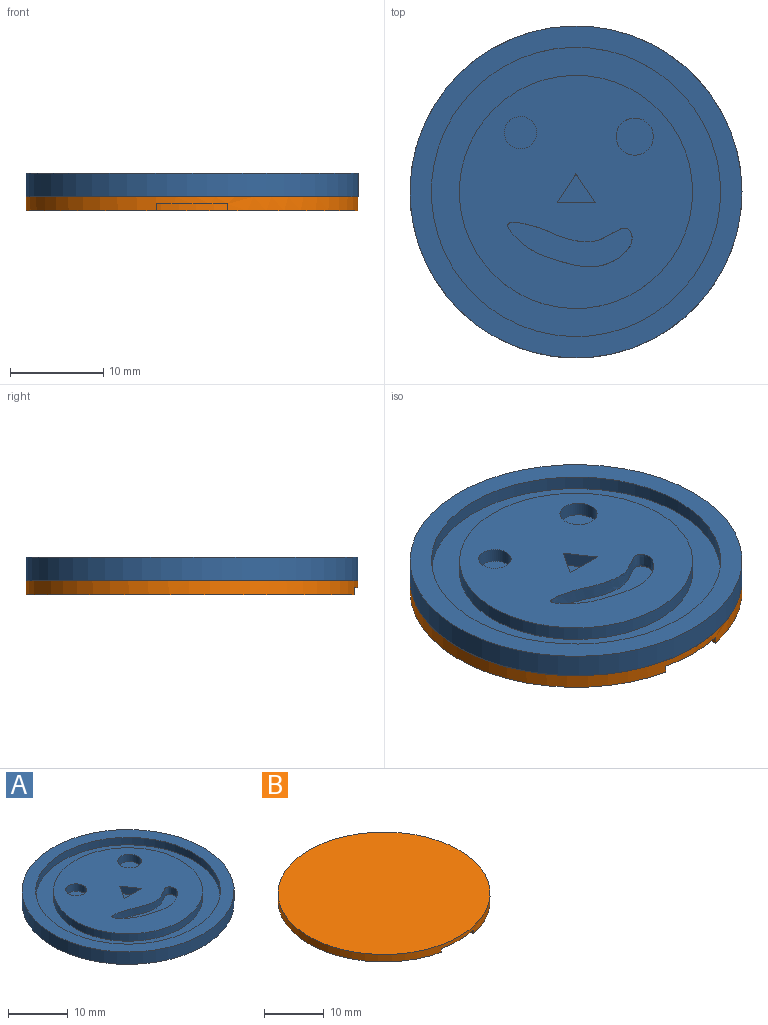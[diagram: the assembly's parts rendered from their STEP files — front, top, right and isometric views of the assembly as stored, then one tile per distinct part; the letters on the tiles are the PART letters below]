
ASSEMBLY  parts=2 mates=1
PART A: 17 faces, bbox 35.6x35.6x2.5 mm
  f0: cylinder r=17.78mm len=35.56mm, axis (0,0,-1), area 283.8mm2, adj f1,f2
  f1: plane 35.56x35.56mm, normal (0,0,1), area 239mm2, adj f0,f3
  f2: plane 35.56x35.56mm, normal (0,0,-1), area 993.1mm2, adj f0
  f3: cylinder r=15.49mm len=30.99mm, axis (0,0,1), area 148.4mm2, adj f1,f4
  f4: plane 30.99x30.99mm, normal (0,0,1), area 264.3mm2, adj f3,f6
  f5: plane 24.98x24.98mm, normal (0,0,1), area 427.8mm2, adj f6,f7,f8,f9,f10,f11,f12
  f6: cylinder r=12.49mm len=24.98mm, axis (0,0,1), area 119.6mm2, adj f4,f5
  f7: plane 3.05x2.03mm, normal (0.83,-0.55,0), area 5.6mm2, adj f5,f8,f9,f14
  f8: plane 3.05x2.07mm, normal (-0.83,-0.56,0), area 5.6mm2, adj f5,f7,f9,f14
  f9: plane 4.1x1.52mm, normal (0,1,0), area 6.2mm2, adj f5,f7,f8,f14
  f10: extruded ~13.3x4.76mm, area 47.1mm2, adj f5,f15
  f11: cylinder r=1.99mm len=3.98mm, axis (0,0,1), area 19mm2, adj f5,f13
  f12: cylinder r=1.74mm len=3.48mm, axis (0,0,1), area 16.6mm2, adj f5,f16
  f13: plane 3.98x3.98mm, normal (0,0,1), area 12.4mm2, adj f11
  f14: plane 4.1x3.05mm, normal (0,0,1), area 6.3mm2, adj f7,f8,f9
  f15: plane 13.65x5.11mm, normal (0,0,1), area 33.9mm2, adj f10
  f16: plane 3.48x3.48mm, normal (0,0,1), area 9.5mm2, adj f12
PART B: 170 faces, bbox 35.6x35.6x1.5 mm
  f0: plane 30.99x30.99mm, normal (0,0,-1), area 549.6mm2, adj f4,f5,f6,f7,f8,f9,f10,f11
  f1: plane 35.56x35.15mm, normal (0,0,-1), area 175mm2, adj f2,f165,f167,f169
  f2: cylinder r=17.78mm len=35.56mm, axis (0,0,-1), area 164.4mm2, adj f1,f3,f165,f167,f168
  f3: plane 35.56x35.56mm, normal (0,0,1), area 993.1mm2, adj f2
  f4: plane 1.49x0.76mm, normal (0,-1,0), area 1.1mm2, adj f0,f5,f15,f16
  f5: plane 7.05x0.76mm, normal (-1,0,0), area 5.4mm2, adj f0,f4,f6,f16
  f6: plane 1.49x0.76mm, normal (0,1,0), area 1.1mm2, adj f0,f5,f7,f16
  f7: plane 2.76x0.76mm, normal (1,0,0), area 2.1mm2, adj f0,f6,f8,f16
  f8: plane 2.79x0.76mm, normal (0,1,0), area 2.1mm2, adj f0,f7,f9,f16
  f9: plane 2.76x0.76mm, normal (-1,0,0), area 2.1mm2, adj f0,f8,f10,f16
  f10: plane 1.5x0.76mm, normal (0,1,0), area 1.1mm2, adj f0,f9,f11,f16
  f11: plane 7.05x0.76mm, normal (1,0,0), area 5.4mm2, adj f0,f10,f12,f16
  f12: plane 1.5x0.76mm, normal (0,-1,0), area 1.1mm2, adj f0,f11,f13,f16
  f13: plane 3.04x0.76mm, normal (-1,0,0), area 2.3mm2, adj f0,f12,f14,f16
  f14: plane 2.79x0.76mm, normal (0,-1,0), area 2.1mm2, adj f0,f13,f15,f16
  f15: plane 3.04x0.76mm, normal (1,0,0), area 2.3mm2, adj f0,f4,f14,f16
  f16: plane 7.05x5.78mm, normal (0,0,-1), area 24.5mm2, adj f4,f5,f6,f7,f8,f9,f10,f11
  f17: plane 7.05x0.76mm, normal (-1,0,0), area 5.4mm2, adj f0,f18,f41,f42
  f18: plane 2.19x0.76mm, normal (0,1,0), area 1.7mm2, adj f0,f17,f19,f42
  f19: extruded ~2.18x0.76mm, area 1.7mm2, adj f0,f18,f20,f42
  f20: extruded ~1.36x0.76mm, area 1.2mm2, adj f0,f19,f21,f42
  f21: extruded ~1.04x0.76mm, area 0.8mm2, adj f0,f20,f22,f42
  f22: extruded ~0.79x0.76mm, area 0.7mm2, adj f0,f21,f23,f42
  f23: plane 0.76x0.05mm, normal (1,0,0), area 0mm2, adj f0,f22,f24,f42
  f24: extruded ~0.97x0.76mm, area 0.9mm2, adj f0,f23,f25,f42
  f25: extruded ~1.09x0.76mm, area 0.9mm2, adj f0,f24,f26,f42
  f26: extruded ~1.51x0.76mm, area 1.3mm2, adj f0,f25,f27,f42
  f27: extruded ~1.89x0.76mm, area 1.5mm2, adj f0,f26,f41,f42
  f28: plane 0.93x0.76mm, normal (0,-1,0), area 0.7mm2, adj f29,f39,f42,f44
  f29: plane 1.84x0.76mm, normal (1,0,0), area 1.4mm2, adj f28,f30,f42,f44
  f30: plane 0.97x0.76mm, normal (0,1,0), area 0.7mm2, adj f29,f31,f42,f44
  f31: extruded ~0.91x0.76mm, area 0.7mm2, adj f30,f32,f42,f44
  f32: extruded ~0.76x0.72mm, area 0.6mm2, adj f31,f39,f42,f44
  f33: plane 1.57x0.76mm, normal (1,0,0), area 1.2mm2, adj f34,f40,f42,f43
  f34: plane 0.87x0.76mm, normal (0,1,0), area 0.7mm2, adj f33,f35,f42,f43
  f35: extruded ~0.88x0.76mm, area 0.7mm2, adj f34,f36,f42,f43
  f36: extruded ~0.76x0.62mm, area 0.5mm2, adj f35,f37,f42,f43
  f37: extruded ~0.76x0.58mm, area 0.5mm2, adj f36,f38,f42,f43
  f38: extruded ~0.94x0.76mm, area 0.7mm2, adj f37,f40,f42,f43
  f39: extruded ~1.25x0.88mm, area 1.3mm2, adj f28,f32,f42,f44
  f40: plane 0.79x0.76mm, normal (0,-1,0), area 0.6mm2, adj f33,f38,f42,f43
  f41: plane 2.64x0.76mm, normal (0,-1,0), area 2mm2, adj f0,f17,f27,f42
  f42: plane 7.05x5.23mm, normal (0,0,-1), area 27.1mm2, adj f17,f18,f19,f20,f21,f22,f23,f24
  f43: plane 2.02x1.57mm, normal (0,0,-1), area 2.9mm2, adj f33,f34,f35,f36,f37,f38,f40
  f44: plane 2.18x1.84mm, normal (0,0,-1), area 3.6mm2, adj f28,f29,f30,f31,f32,f39
  f45: extruded ~2.44x2.09mm, area 2.8mm2, adj f0,f46,f52,f53
  f46: extruded ~2.44x2.09mm, area 2.8mm2, adj f0,f45,f47,f53
  f47: extruded ~2.41x2.09mm, area 2.7mm2, adj f0,f46,f52,f53
  f48: extruded ~1.63x1.14mm, area 1.7mm2, adj f49,f51,f53,f54
  f49: extruded ~1.63x1.14mm, area 1.7mm2, adj f48,f50,f53,f54
  f50: extruded ~1.6x1.14mm, area 1.7mm2, adj f49,f51,f53,f54
  f51: extruded ~1.6x1.14mm, area 1.7mm2, adj f48,f50,f53,f54
  f52: extruded ~2.41x2.09mm, area 2.7mm2, adj f0,f45,f47,f53
  f53: plane 4.85x4.18mm, normal (0,0,-1), area 10.4mm2, adj f45,f46,f47,f48,f49,f50,f51,f52
  f54: plane 3.24x2.27mm, normal (0,0,-1), area 6mm2, adj f48,f49,f50,f51
  f55: extruded ~1.45x0.82mm, area 1.3mm2, adj f0,f56,f62,f63
  f56: extruded ~1.6x1.45mm, area 1.9mm2, adj f0,f55,f57,f63
  f57: plane 3.16x0.76mm, normal (-1,0,0), area 2.4mm2, adj f0,f56,f58,f63
  f58: plane 0.93x0.76mm, normal (0,1,0), area 0.7mm2, adj f0,f57,f59,f63
  f59: plane 3.09x0.76mm, normal (1,0,0), area 2.4mm2, adj f0,f58,f60,f63
  f60: extruded ~0.86x0.76mm, area 0.9mm2, adj f0,f59,f61,f63
  f61: extruded ~0.76x0.69mm, area 0.7mm2, adj f0,f60,f62,f63
  f62: plane 0.76x0.64mm, normal (0.59,0.81,0), area 0.6mm2, adj f0,f55,f61,f63
  f63: plane 4.76x2.9mm, normal (0,0,-1), area 5.6mm2, adj f55,f56,f57,f58,f59,f60,f61,f62
  f64: extruded ~2.19x1.82mm, area 2.5mm2, adj f0,f65,f73,f74
  f65: extruded ~2.19x1.81mm, area 2.5mm2, adj f0,f64,f66,f74
  f66: plane 2.57x0.76mm, normal (-1,0,0), area 2mm2, adj f0,f65,f67,f74
  f67: plane 0.9x0.76mm, normal (0,1,0), area 0.7mm2, adj f0,f66,f68,f74
  f68: plane 2.65x0.76mm, normal (1,0,0), area 2mm2, adj f0,f67,f69,f74
  f69: extruded ~1.3x0.91mm, area 1.4mm2, adj f0,f68,f70,f74
  f70: extruded ~1.3x0.88mm, area 1.4mm2, adj f0,f69,f71,f74
  f71: plane 2.65x0.76mm, normal (-1,0,0), area 2mm2, adj f0,f70,f72,f74
  f72: plane 0.93x0.76mm, normal (0,1,0), area 0.7mm2, adj f0,f71,f73,f74
  f73: plane 2.57x0.76mm, normal (1,0,0), area 2mm2, adj f0,f64,f72,f74
  f74: plane 4.76x3.62mm, normal (0,0,-1), area 9.2mm2, adj f64,f65,f66,f67,f68,f69,f70,f71
  f75: plane 4.67x0.76mm, normal (1,0,0), area 3.6mm2, adj f0,f76,f90,f91
  f76: plane 0.88x0.76mm, normal (0,-1,0), area 0.7mm2, adj f0,f75,f77,f91
  f77: plane 1.88x0.76mm, normal (-1,0,0), area 1.4mm2, adj f0,f76,f78,f91
  f78: extruded ~1.63x0.76mm, area 1.2mm2, adj f0,f77,f79,f91
  f79: plane 0.76x0.03mm, normal (0,-1,0), area 0mm2, adj f0,f78,f80,f91
  f80: plane 1x0.76mm, normal (0.9,-0.43,0), area 0.8mm2, adj f0,f79,f81,f91
  f81: plane 2.5x1.35mm, normal (0.88,-0.48,0), area 2.2mm2, adj f0,f80,f82,f91
  f82: plane 0.95x0.76mm, normal (0,-1,0), area 0.7mm2, adj f0,f81,f83,f91
  f83: plane 4.67x0.76mm, normal (-1,0,0), area 3.6mm2, adj f0,f82,f84,f91
  f84: plane 0.88x0.76mm, normal (0,1,0), area 0.7mm2, adj f0,f83,f85,f91
  f85: plane 1.86x0.76mm, normal (1,0,0), area 1.4mm2, adj f0,f84,f86,f91
  f86: extruded ~1.64x0.76mm, area 1.3mm2, adj f0,f85,f87,f91
  f87: plane 0.76x0.03mm, normal (0,1,0), area 0mm2, adj f0,f86,f88,f91
  f88: plane 1.01x0.76mm, normal (-0.91,0.42,0), area 0.8mm2, adj f0,f87,f89,f91
  f89: plane 2.49x1.36mm, normal (-0.88,0.48,0), area 2.2mm2, adj f0,f88,f90,f91
  f90: plane 0.95x0.76mm, normal (0,1,0), area 0.7mm2, adj f0,f75,f89,f91
  f91: plane 4.67x3.57mm, normal (0,0,-1), area 10.9mm2, adj f75,f76,f77,f78,f79,f80,f81,f82
  f92: plane 2.41x1.31mm, normal (0.88,0.48,0), area 2.1mm2, adj f0,f93,f109,f110
  f93: plane 0.99x0.76mm, normal (0,-1,0), area 0.8mm2, adj f0,f92,f94,f110
  f94: plane 1.04x0.76mm, normal (-0.9,-0.43,0), area 0.9mm2, adj f0,f93,f95,f110
  f95: extruded ~0.77x0.76mm, area 0.6mm2, adj f0,f94,f96,f110
  f96: plane 0.76x0.02mm, normal (0,-1,0), area 0mm2, adj f0,f95,f97,f110
  f97: extruded ~0.77x0.76mm, area 0.6mm2, adj f0,f96,f98,f110
  f98: plane 1.04x0.76mm, normal (0.89,-0.45,0), area 0.9mm2, adj f0,f97,f99,f110
  f99: plane 1.04x0.76mm, normal (0,-1,0), area 0.8mm2, adj f0,f98,f100,f110
  f100: plane 2.37x1.31mm, normal (-0.87,0.48,0), area 2.1mm2, adj f0,f99,f101,f110
  f101: plane 2.3x1.23mm, normal (-0.88,-0.47,0), area 2mm2, adj f0,f100,f102,f110
  f102: plane 0.98x0.76mm, normal (0,1,0), area 0.8mm2, adj f0,f101,f103,f110
  f103: plane 0.96x0.76mm, normal (0.91,0.42,0), area 0.8mm2, adj f0,f102,f104,f110
  f104: extruded ~0.76x0.74mm, area 0.6mm2, adj f0,f103,f105,f110
  f105: plane 0.76x0.03mm, normal (0,1,0), area 0mm2, adj f0,f104,f106,f110
  f106: extruded ~0.76x0.74mm, area 0.6mm2, adj f0,f105,f107,f110
  f107: plane 0.96x0.76mm, normal (-0.9,0.44,0), area 0.8mm2, adj f0,f106,f108,f110
  f108: plane 1.04x0.76mm, normal (0,1,0), area 0.8mm2, adj f0,f107,f109,f110
  f109: plane 2.26x1.23mm, normal (0.88,-0.48,0), area 2mm2, adj f0,f92,f108,f110
  f110: plane 4.67x3.78mm, normal (0,0,-1), area 8.4mm2, adj f92,f93,f94,f95,f96,f97,f98,f99
  f111: plane 4.67x0.76mm, normal (1,0,0), area 3.6mm2, adj f0,f112,f114,f115
  f112: plane 0.94x0.76mm, normal (0,-1,0), area 0.7mm2, adj f0,f111,f113,f115
  f113: plane 4.67x0.76mm, normal (-1,0,0), area 3.6mm2, adj f0,f112,f114,f115
  f114: plane 0.94x0.76mm, normal (0,1,0), area 0.7mm2, adj f0,f111,f113,f115
  f115: plane 4.67x0.94mm, normal (0,0,-1), area 4.4mm2, adj f111,f112,f113,f114
  f116: plane 4.67x0.76mm, normal (1,0,0), area 3.6mm2, adj f0,f117,f131,f132
  f117: plane 0.88x0.76mm, normal (0,-1,0), area 0.7mm2, adj f0,f116,f118,f132
  f118: plane 1.88x0.76mm, normal (-1,0,0), area 1.4mm2, adj f0,f117,f119,f132
  f119: extruded ~1.63x0.76mm, area 1.2mm2, adj f0,f118,f120,f132
  f120: plane 0.76x0.03mm, normal (0,-1,0), area 0mm2, adj f0,f119,f121,f132
  f121: plane 1x0.76mm, normal (0.9,-0.43,0), area 0.8mm2, adj f0,f120,f122,f132
  f122: plane 2.5x1.35mm, normal (0.88,-0.48,0), area 2.2mm2, adj f0,f121,f123,f132
  f123: plane 0.95x0.76mm, normal (0,-1,0), area 0.7mm2, adj f0,f122,f124,f132
  f124: plane 4.67x0.76mm, normal (-1,0,0), area 3.6mm2, adj f0,f123,f125,f132
  f125: plane 0.88x0.76mm, normal (0,1,0), area 0.7mm2, adj f0,f124,f126,f132
  f126: plane 1.86x0.76mm, normal (1,0,0), area 1.4mm2, adj f0,f125,f127,f132
  f127: extruded ~1.64x0.76mm, area 1.3mm2, adj f0,f126,f128,f132
  f128: plane 0.76x0.03mm, normal (0,1,0), area 0mm2, adj f0,f127,f129,f132
  f129: plane 1.01x0.76mm, normal (-0.91,0.42,0), area 0.8mm2, adj f0,f128,f130,f132
  f130: plane 2.49x1.36mm, normal (-0.88,0.48,0), area 2.2mm2, adj f0,f129,f131,f132
  f131: plane 0.95x0.76mm, normal (0,1,0), area 0.7mm2, adj f0,f116,f130,f132
  f132: plane 4.67x3.57mm, normal (0,0,-1), area 10.9mm2, adj f116,f117,f118,f119,f120,f121,f122,f123
  f133: extruded ~1.78x0.76mm, area 1.4mm2, adj f134,f146,f147,f163
  f134: extruded ~1.78x0.76mm, area 1.4mm2, adj f133,f135,f147,f163
  f135: extruded ~1.35x0.76mm, area 1.2mm2, adj f134,f136,f147,f163
  f136: extruded ~2.38x1.78mm, area 2.6mm2, adj f135,f137,f147,f163
  f137: extruded ~2.38x1.79mm, area 2.6mm2, adj f136,f146,f147,f163
  f138: extruded ~2.69x0.87mm, area 2.2mm2, adj f0,f139,f145,f147
  f139: extruded ~2.69x0.86mm, area 2.2mm2, adj f0,f138,f140,f147
  f140: extruded ~2.49x0.94mm, area 2.1mm2, adj f0,f139,f141,f147
  f141: extruded ~2.5x0.93mm, area 2.1mm2, adj f0,f140,f142,f147
  f142: extruded ~2.69x0.87mm, area 2.2mm2, adj f0,f141,f143,f147
  f143: extruded ~2.7x0.87mm, area 2.2mm2, adj f0,f142,f144,f147
  f144: extruded ~2.49x0.94mm, area 2.1mm2, adj f0,f143,f145,f147
  f145: extruded ~2.49x0.94mm, area 2.1mm2, adj f0,f138,f144,f147
  f146: extruded ~1.34x0.76mm, area 1.2mm2, adj f133,f137,f147,f163
  f147: plane 7.26x6.71mm, normal (0,0,-1), area 26mm2, adj f133,f134,f135,f136,f137,f138,f139,f140
  f148: extruded ~1.78x0.76mm, area 1.4mm2, adj f149,f161,f162,f164
  f149: extruded ~1.78x0.76mm, area 1.4mm2, adj f148,f150,f162,f164
  f150: extruded ~1.35x0.76mm, area 1.2mm2, adj f149,f151,f162,f164
  f151: extruded ~2.38x1.78mm, area 2.6mm2, adj f150,f152,f162,f164
  f152: extruded ~2.38x1.79mm, area 2.6mm2, adj f151,f161,f162,f164
  f153: extruded ~2.69x0.87mm, area 2.2mm2, adj f0,f154,f160,f162
  f154: extruded ~2.69x0.86mm, area 2.2mm2, adj f0,f153,f155,f162
  f155: extruded ~2.49x0.94mm, area 2.1mm2, adj f0,f154,f156,f162
  f156: extruded ~2.5x0.93mm, area 2.1mm2, adj f0,f155,f157,f162
  f157: extruded ~2.69x0.87mm, area 2.2mm2, adj f0,f156,f158,f162
  f158: extruded ~2.7x0.87mm, area 2.2mm2, adj f0,f157,f159,f162
  f159: extruded ~2.49x0.94mm, area 2.1mm2, adj f0,f158,f160,f162
  f160: extruded ~2.49x0.94mm, area 2.1mm2, adj f0,f153,f159,f162
  f161: extruded ~1.34x0.76mm, area 1.2mm2, adj f148,f152,f162,f164
  f162: plane 7.26x6.71mm, normal (0,0,-1), area 26mm2, adj f148,f149,f150,f151,f152,f153,f154,f155
  f163: plane 4.76x3.58mm, normal (0,0,-1), area 14.2mm2, adj f133,f134,f135,f136,f137,f146
  f164: plane 4.76x3.58mm, normal (0,0,-1), area 14.2mm2, adj f148,f149,f150,f151,f152,f161
  f165: plane 1.83x0.76mm, normal (1,0,0), area 1.4mm2, adj f1,f2,f168,f169
  f166: cylinder r=15.49mm len=30.99mm, axis (0,0,-1), area 74.2mm2, adj f0,f168
  f167: plane 1.83x0.76mm, normal (-1,0,0), area 1.4mm2, adj f1,f2,f168,f169
  f168: plane 33.78x32mm, normal (0,0,-1), area 63.9mm2, adj f2,f165,f166,f167,f169
  f169: cylinder r=16mm len=32mm, axis (0,0,-1), area 70.8mm2, adj f1,f165,f167,f168
PLACE A t=(-6.45,-25.08,-32.14)mm fixed
PLACE B t=(-6.45,-25.08,-33.67)mm
MATE fastened B.f2 <-> A.f0  axis (0,0,1) through (-6.45,-25.08,-32.14)mm
